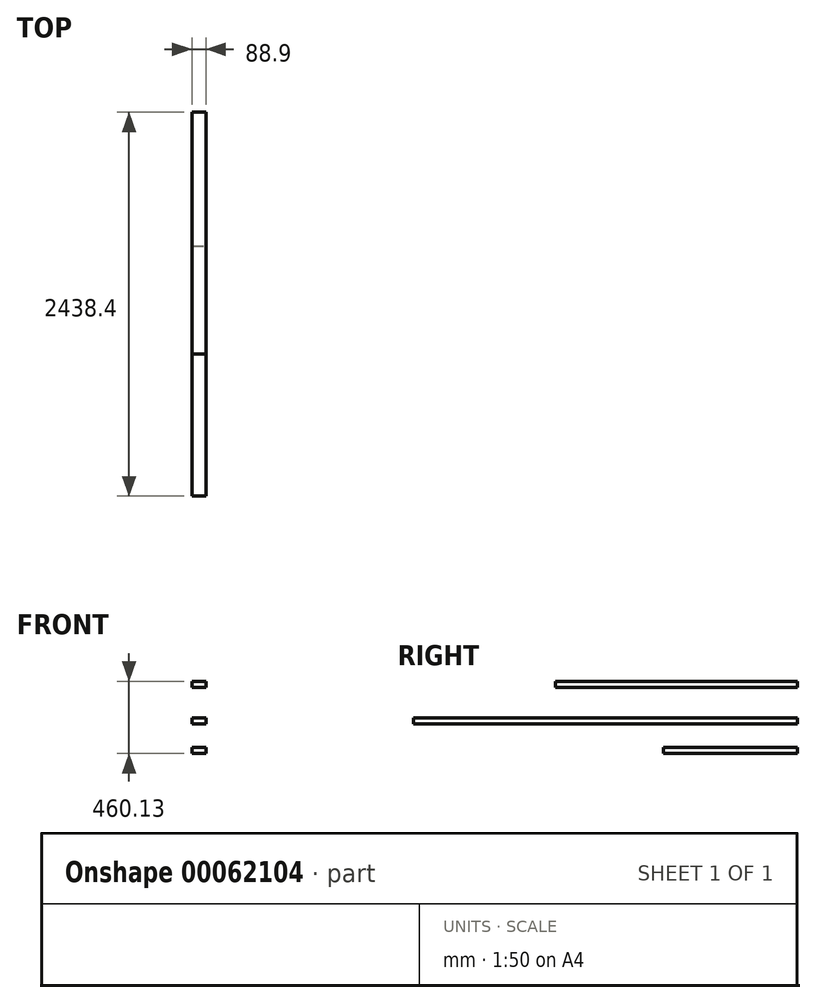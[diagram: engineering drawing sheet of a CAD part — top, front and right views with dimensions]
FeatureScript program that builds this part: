
annotation { "Feature Type Name" : "Feature", "Feature Type Description" : "" }
export const myFeature = defineFeature(function(context is Context, id is Id, definition is map)
    precondition{}
    {
        {
            var Q0;
            Q0=qCreatedBy(makeId("Front.planeOp"),FACE);
            var sketch = newSketch(context, id + "F0", { "sketchPlane" : qUnion([Q0])});
            skLineSegment(sketch, "E0", {"start": v(0, 0) * mm, "end": v(0, 121.71) * mm, "construction": true});
            skLineSegment(sketch, "E1", {"start": v(0, 0) * mm, "end": v(110.24, 0) * mm, "construction": true});
            skLineSegment(sketch, "E2.bottom", {"start": v(-44.45, 19.05) * mm, "end": v(44.45, 19.05) * mm});
            skLineSegment(sketch, "E2.top", {"start": v(-44.45, -19.05) * mm, "end": v(44.45, -19.05) * mm});
            skLineSegment(sketch, "E2.left", {"start": v(-44.45, 19.05) * mm, "end": v(-44.45, -19.05) * mm});
            skLineSegment(sketch, "E2.right", {"start": v(44.45, 19.05) * mm, "end": v(44.45, -19.05) * mm});
            skSolve(sketch);
        }
        {
            var Q0;
            Q0=makeQuery(id+"F0.imprint","IMPRINT",FACE,{"disambiguationData":[TD([[makeQuery(id+"F0.imprint","IMPRINT",EDGE,{"derivedFrom":sQuery(id+"F0.wireOp",EDGE,"E2.bottom")}),-1.0]])]});
            extrude(context, id + "F1", {"entities" : qUnion([Q0]), "endBound" : BoundingType.SYMMETRIC, "depth" : 850.9 * mm});
        }
        {
            var Q0;
            Q0=makeQuery(id+"F1.opExtrude","SWEPT_BODY",BODY,{"disambiguationData":[OSD([sQuery(id+"F0.wireOp",EDGE,"E2.bottom"),sQuery(id+"F0.wireOp",EDGE,"E2.top"),sQuery(id+"F0.wireOp",EDGE,"E2.left"),sQuery(id+"F0.wireOp",EDGE,"E2.right")])]});
            transform(context, id + "F2", {"entities" : qUnion([Q0]), "transformType" : TransformType.TRANSLATION_3D, "dx" : 0 * mm, "dy" : 0 * mm, "dz" : 187.32 * mm, "makeCopy" : true});
        }
        {
            var Q0;
            Q0=makeQuery(id+"F2.opPattern","COPY",FACE,{"derivedFrom":makeQuery(id+"F1.opExtrude","CAP_FACE",FACE,{"disambiguationData":[OSD([sQuery(id+"F0.wireOp",EDGE,"E2.bottom"),sQuery(id+"F0.wireOp",EDGE,"E2.top"),sQuery(id+"F0.wireOp",EDGE,"E2.left"),sQuery(id+"F0.wireOp",EDGE,"E2.right")])],"isStart":false}),"instanceName":"1"});
            extrude(context, id + "F3", {"entities" : qUnion([Q0]), "operationType" : NewBodyOperationType.ADD, "depth" : 1587.5 * mm});
        }
        {
            var Q0;
            Q0=makeQuery(id+"F1.opExtrude","SWEPT_BODY",BODY,{"disambiguationData":[OSD([sQuery(id+"F0.wireOp",EDGE,"E2.bottom"),sQuery(id+"F0.wireOp",EDGE,"E2.top"),sQuery(id+"F0.wireOp",EDGE,"E2.left"),sQuery(id+"F0.wireOp",EDGE,"E2.right")])]});
            transform(context, id + "F4", {"entities" : qUnion([Q0]), "transformType" : TransformType.TRANSLATION_3D, "dx" : 0 * mm, "dy" : 0 * mm, "dz" : 422.03 * mm, "makeCopy" : true});
        }
        {
            var Q0;
            Q0=makeQuery(id+"F4.opPattern","COPY",FACE,{"derivedFrom":makeQuery(id+"F1.opExtrude","CAP_FACE",FACE,{"disambiguationData":[OSD([sQuery(id+"F0.wireOp",EDGE,"E2.bottom"),sQuery(id+"F0.wireOp",EDGE,"E2.top"),sQuery(id+"F0.wireOp",EDGE,"E2.left"),sQuery(id+"F0.wireOp",EDGE,"E2.right")])],"isStart":false}),"instanceName":"1"});
            extrude(context, id + "F5", {"entities" : qUnion([Q0]), "operationType" : NewBodyOperationType.ADD, "depth" : 685.8 * mm});
        }
    });
